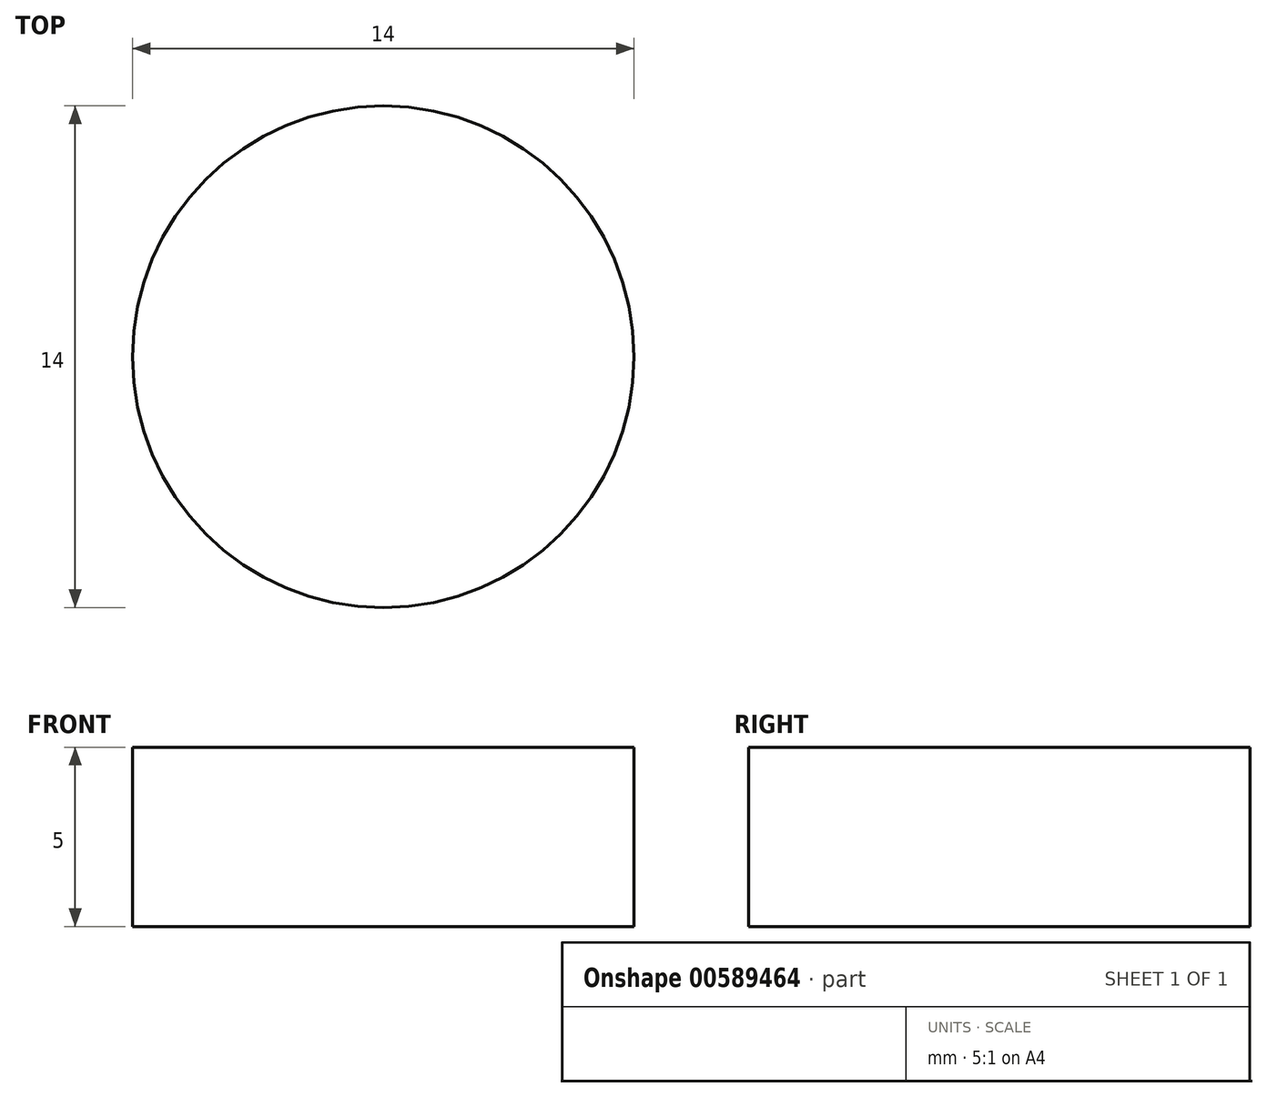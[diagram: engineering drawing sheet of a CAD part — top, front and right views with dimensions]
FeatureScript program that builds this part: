
annotation { "Feature Type Name" : "Feature", "Feature Type Description" : "" }
export const myFeature = defineFeature(function(context is Context, id is Id, definition is map)
    precondition{}
    {
        {
            var Q0;
            Q0=qCreatedBy(makeId("Top.planeOp"),FACE);
            var sketch = newSketch(context, id + "F0", { "sketchPlane" : qUnion([Q0])});
            skCircle(sketch, "E0", {"center": v(0, 0) * mm, "radius": 7 * mm});
            skSolve(sketch);
        }
        {
            var Q0;
            Q0=makeQuery(id+"F0.imprint","IMPRINT",FACE,{"disambiguationData":[TD([[makeQuery(id+"F0.imprint","IMPRINT",EDGE,{"derivedFrom":sQuery(id+"F0.wireOp",EDGE,"E0")}),1.0]])]});
            extrude(context, id + "F1", {"entities" : qUnion([Q0]), "depth" : 5 * mm, "offsetDistance" : 25 * mm});
        }
        {
            var Q0;
            Q0=qCreatedBy(makeId("Top.planeOp"),FACE);
            var sketch = newSketch(context, id + "F2", { "sketchPlane" : qUnion([Q0])});
            skCircle(sketch, "E1", {"center": v(0, 0) * mm, "radius": 7 * mm});
            skSolve(sketch);
        }
        {
            var Q0;
            Q0 = qSketchRegion(id + "F2", true);
            extrude(context, id + "F3", {"entities" : qUnion([Q0]), "operationType" : NewBodyOperationType.ADD, "oppositeDirection" : true, "depth" : 5 * mm, "offsetDistance" : 25 * mm});
        }
        {
            var Q0;
            Q0=makeQuery(id+"F1.opExtrude","CAP_FACE",FACE,{"disambiguationData":[OSD([sQuery(id+"F0.wireOp",EDGE,"E0")])],"isStart":false});
            extrude(context, id + "F4", {"entities" : qUnion([Q0]), "operationType" : NewBodyOperationType.REMOVE, "oppositeDirection" : true, "depth" : 5 * mm, "offsetDistance" : 25 * mm});
        }
    });
